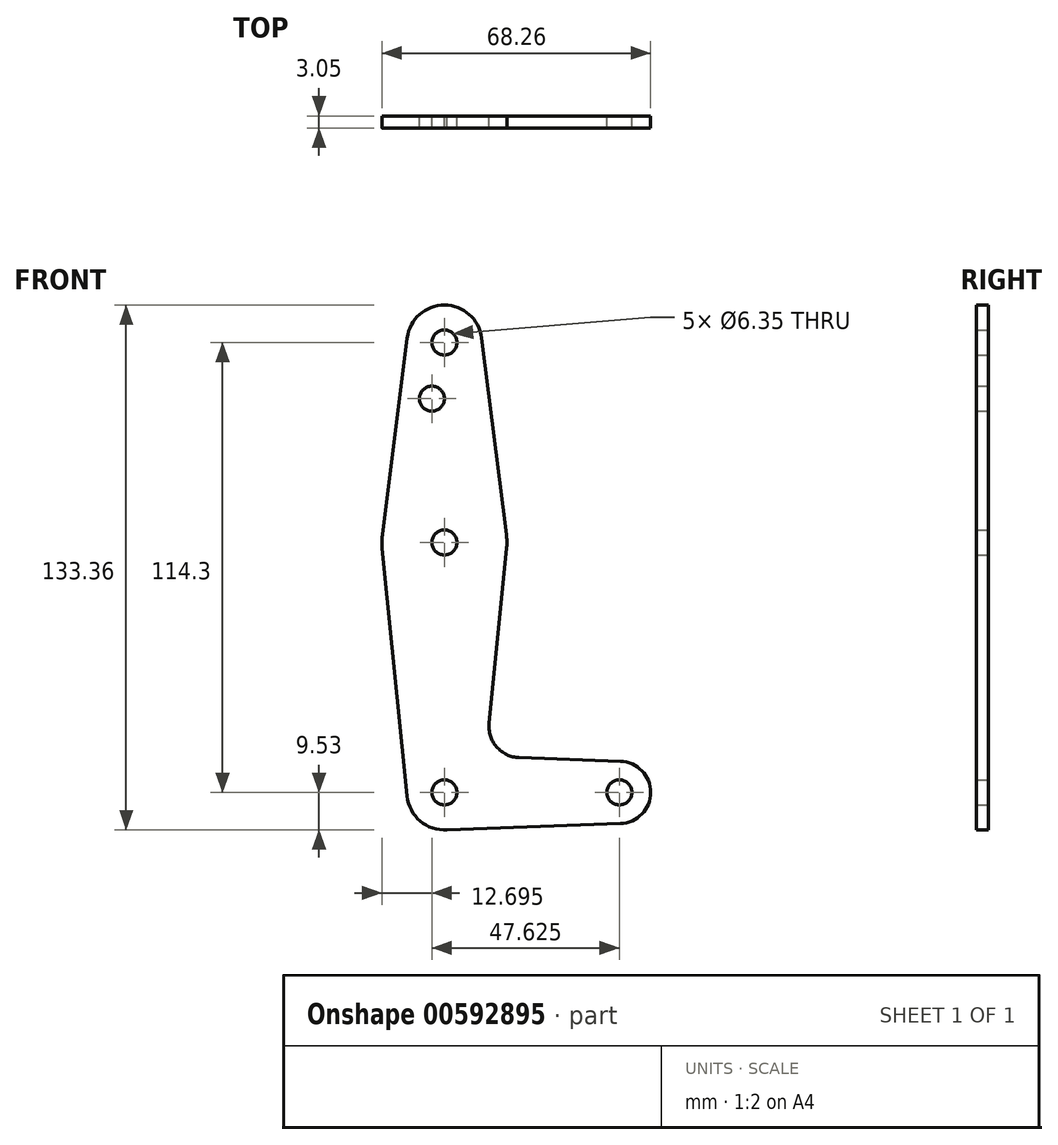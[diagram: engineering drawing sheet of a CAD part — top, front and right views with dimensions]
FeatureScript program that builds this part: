
annotation { "Feature Type Name" : "Feature", "Feature Type Description" : "" }
export const myFeature = defineFeature(function(context is Context, id is Id, definition is map)
    precondition{}
    {
        {
            var Q0;
            Q0=qCreatedBy(makeId("Front.planeOp"),FACE);
            var sketch = newSketch(context, id + "F0", { "sketchPlane" : qUnion([Q0])});
            skLineSegment(sketch, "E0", {"start": v(0, 0) * mm, "end": v(0, 114.3) * mm, "construction": true});
            skLineSegment(sketch, "E1", {"start": v(0, 0) * mm, "end": v(44.45, 0) * mm, "construction": true});
            skCircle(sketch, "E2", {"center": v(0, 114.3) * mm, "radius": 9.53 * mm});
            skCircle(sketch, "E3", {"center": v(0, 63.5) * mm, "radius": 15.88 * mm});
            skCircle(sketch, "E4", {"center": v(0, 0) * mm, "radius": 9.53 * mm});
            skCircle(sketch, "E5", {"center": v(44.45, 0) * mm, "radius": 7.94 * mm});
            skLineSegment(sketch, "E6", {"start": v(-9.45, 115.5) * mm, "end": v(-15.75, 65.48) * mm});
            skLineSegment(sketch, "E7", {"start": v(15.75, 65.48) * mm, "end": v(9.45, 115.5) * mm});
            skLineSegment(sketch, "E8", {"start": v(-15.8, 61.91) * mm, "end": v(-9.48, -0.95) * mm});
            skLineSegment(sketch, "E9", {"start": v(11.34, 17.59) * mm, "end": v(15.8, 61.91) * mm});
            skLineSegment(sketch, "E10", {"start": v(18.97, 8.85) * mm, "end": v(44.73, 7.93) * mm});
            skLineSegment(sketch, "E11", {"start": v(0, -9.53) * mm, "end": v(44.73, -7.93) * mm});
            skCircle(sketch, "E12", {"center": v(0, 0) * mm, "radius": 3.18 * mm});
            skCircle(sketch, "E13", {"center": v(0, 63.5) * mm, "radius": 3.18 * mm});
            skCircle(sketch, "E14", {"center": v(0, 114.3) * mm, "radius": 3.18 * mm});
            skCircle(sketch, "E15", {"center": v(44.45, 0) * mm, "radius": 3.18 * mm});
            skCircle(sketch, "E16", {"center": v(-3.18, 100.03) * mm, "radius": 3.18 * mm});
            skArc(sketch, "E17.filletArc", {"start": v(11.34, 17.59) * mm, "mid": v(13.26, 11.57) * mm, "end": v(18.97, 8.85) * mm});
            skSolve(sketch);
        }
        {
            var Q0;
            Q0 = qSketchRegion(id + "F0", true);
            extrude(context, id + "F1", {"entities" : qUnion([Q0]), "depth" : 3.05 * mm, "offsetDistance" : 25.4 * mm});
        }
    });
